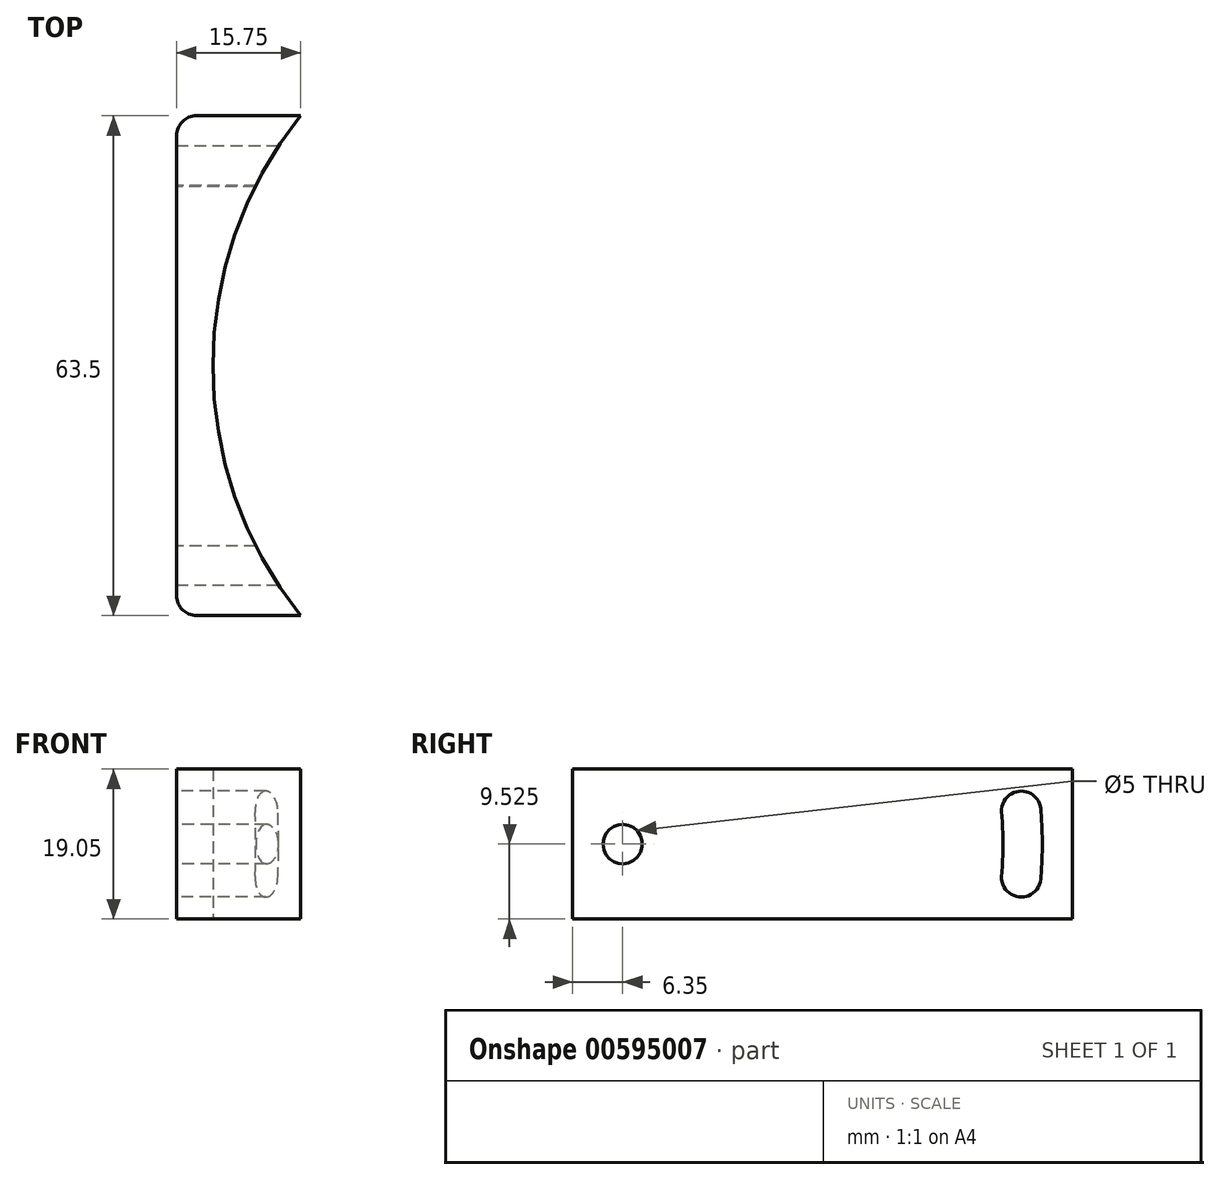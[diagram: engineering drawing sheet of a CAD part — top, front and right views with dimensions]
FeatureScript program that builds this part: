
annotation { "Feature Type Name" : "Feature", "Feature Type Description" : "" }
export const myFeature = defineFeature(function(context is Context, id is Id, definition is map)
    precondition{}
    {
        {
            var Q0;
            Q0=qCreatedBy(makeId("Top.planeOp"),FACE);
            var sketch = newSketch(context, id + "F0", { "sketchPlane" : qUnion([Q0])});
            skArc(sketch, "E0", {"start": v(-39.66, 31.75) * mm, "mid": v(-50.8, 0) * mm, "end": v(-39.66, -31.75) * mm});
            skLineSegment(sketch, "E1", {"start": v(-55.4, 29.21) * mm, "end": v(-55.4, -29.21) * mm});
            skPoint(sketch, "E2", {"position": v(-55.4, 0) * mm});
            skLineSegment(sketch, "E3", {"start": v(-52.87, 31.75) * mm, "end": v(-39.66, 31.75) * mm});
            skLineSegment(sketch, "E4", {"start": v(-52.87, -31.75) * mm, "end": v(-39.66, -31.75) * mm});
            skPoint(sketch, "E5.visualSharp", {"position": v(-55.4, 31.75) * mm});
            skArc(sketch, "E5.filletArc", {"start": v(-52.87, 31.75) * mm, "mid": v(-54.67, 31) * mm, "end": v(-55.4, 29.21) * mm});
            skPoint(sketch, "E6.visualSharp", {"position": v(-55.4, -31.75) * mm});
            skArc(sketch, "E6.filletArc", {"start": v(-55.4, -29.21) * mm, "mid": v(-54.67, -31) * mm, "end": v(-52.87, -31.75) * mm});
            skSolve(sketch);
        }
        {
            var Q0;
            Q0=makeQuery(id+"F0.imprint","IMPRINT",FACE,{"disambiguationData":[TD([[makeQuery(id+"F0.imprint","IMPRINT",EDGE,{"derivedFrom":sQuery(id+"F0.wireOp",EDGE,"E0")}),-1.0]])]});
            extrude(context, id + "F1", {"entities" : qUnion([Q0]), "depth" : 19.05 * mm, "offsetDistance" : 25.4 * mm});
        }
        {
            var Q0;
            Q0=makeQuery(id+"F1.opExtrude","SWEPT_FACE",FACE,{"disambiguationData":[OSD([sQuery(id+"F0.wireOp",EDGE,"E1")])]});
            cPlane(context, id + "F2", {"entities" : qUnion([Q0]), "cplaneType" : CPlaneType.OFFSET, "offset" : 0 * mm, "width" : 152.4 * mm, "height" : 152.4 * mm});
        }
        {
            var Q0;
            Q0=qCreatedBy(id+"F2.planeOp",FACE);
            var sketch = newSketch(context, id + "F3", { "sketchPlane" : qUnion([Q0])});
            skLineSegment(sketch, "E7", {"start": v(-31.75, 19.05) * mm, "end": v(-31.75, 0) * mm});
            skPoint(sketch, "E8", {"position": v(-31.75, 9.53) * mm});
            skLineSegment(sketch, "E9", {"start": v(-31.75, 9.53) * mm, "end": v(26.81, 9.53) * mm});
            skPoint(sketch, "E10", {"position": v(-25.4, 9.53) * mm});
            skPoint(sketch, "E11", {"position": v(25.4, 9.53) * mm});
            skArc(sketch, "E12", {"start": v(-22.73, 13.55) * mm, "mid": v(-25.02, 16.25) * mm, "end": v(-27.72, 13.97) * mm});
            skArc(sketch, "E13.MirrorCS", {"start": v(-22.73, 5.5) * mm, "mid": v(-25.02, 2.8) * mm, "end": v(-27.72, 5.08) * mm});
            skPoint(sketch, "E14.MirrorCS.end.orphan", {"position": v(-27.9, 9.53) * mm});
            skPoint(sketch, "E14.MirrorCS.start.orphan", {"position": v(-27.72, 5.08) * mm});
            skPoint(sketch, "E15.MirrorCS.end.orphan", {"position": v(-22.9, 9.53) * mm});
            skPoint(sketch, "E15.MirrorCS.start.orphan", {"position": v(-22.73, 5.5) * mm});
            skArc(sketch, "E16", {"start": v(-22.73, 13.55) * mm, "mid": v(-22.9, 9.53) * mm, "end": v(-22.73, 5.5) * mm});
            skArc(sketch, "E17", {"start": v(-27.72, 13.97) * mm, "mid": v(-27.9, 9.53) * mm, "end": v(-27.72, 5.08) * mm});
            skSolve(sketch);
        }
        {
            var Q0;
            Q0=sQuery(id+"F3.wireOp",VERTEX,"E11");
            var Q1;
            Q1=makeQuery(id+"F1.opExtrude","SWEPT_BODY",BODY,{"disambiguationData":[OSD([sQuery(id+"F0.wireOp",EDGE,"E0"),sQuery(id+"F0.wireOp",EDGE,"E1"),sQuery(id+"F0.wireOp",EDGE,"E3"),sQuery(id+"F0.wireOp",EDGE,"E4")])]});
            hole(context, id + "F4", {"style" : HoleStyle.SIMPLE, "endStyle" : HoleEndStyle.BLIND, "standardTappedOrClearance" : lookupTablePath({ "standard" : "ISO", "engagement" : "75%", "pitch" : "1 mm", "size" : "M6", "type" : "Tapped" }), "standardBlindInLast" : lookupTablePath({ "standard" : "ISO", "engagement" : "75%", "pitch" : "1 mm", "size" : "M6", "type" : "Tapped" }), "holeDiameter" : 5 * mm, "showTappedDepth" : true, "holeDepth" : 15.7 * mm, "isTappedThrough" : true, "tappedDepth" : 12.7 * mm, "tapClearance" : 3, "locations" : qUnion([Q0]), "scope" : qUnion([Q1]), "majorDiameter" : 6 * mm});
        }
        {
            var Q0;
            Q0=qSketchRegion(id+"F3",true);
            extrude(context, id + "F5", {"entities" : qUnion([Q0]), "operationType" : NewBodyOperationType.REMOVE, "oppositeDirection" : true, "depth" : 25.4 * mm, "offsetDistance" : 25.4 * mm});
        }
    });
